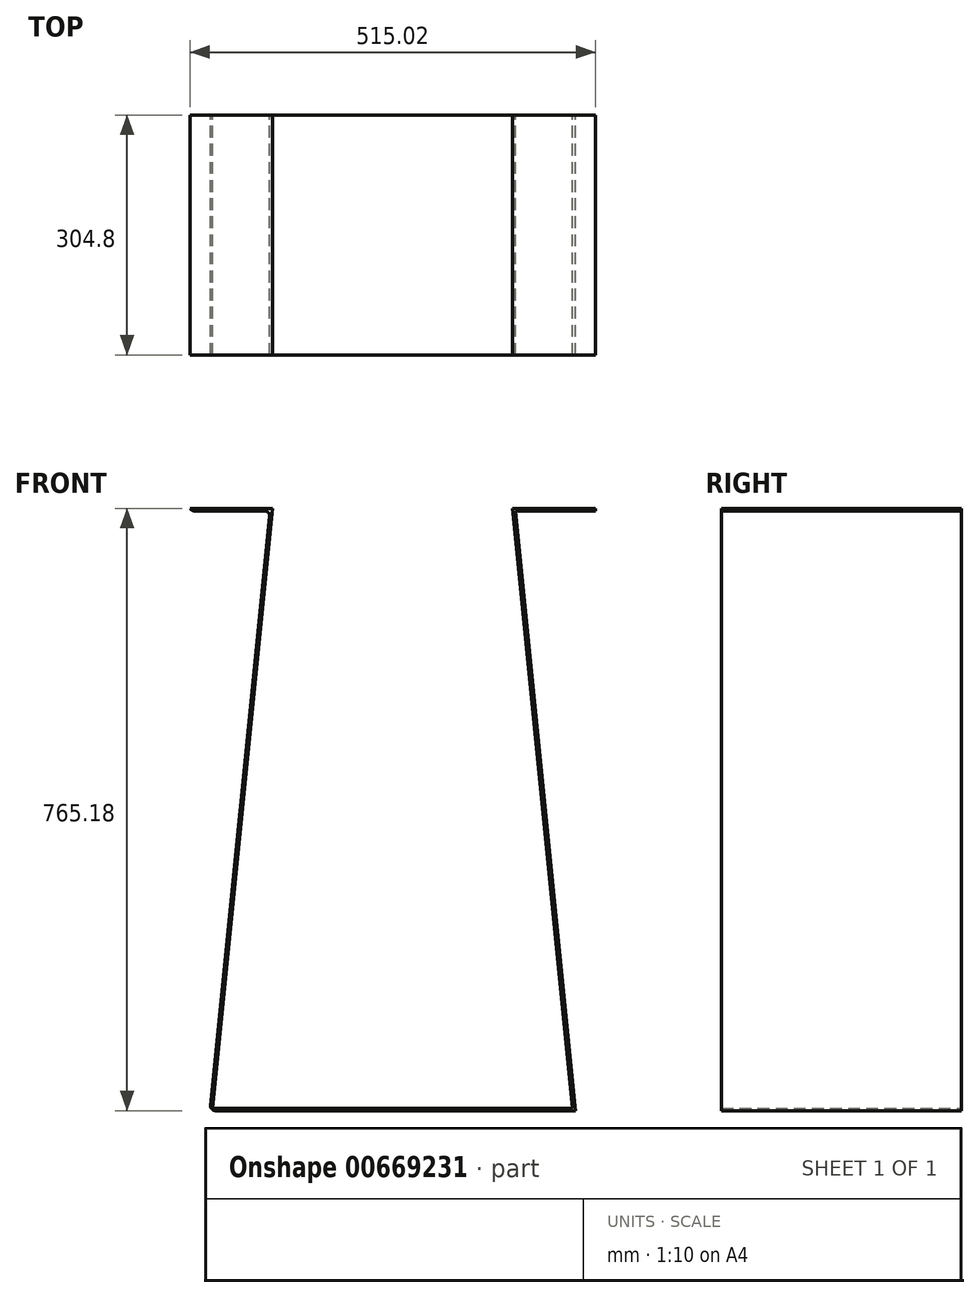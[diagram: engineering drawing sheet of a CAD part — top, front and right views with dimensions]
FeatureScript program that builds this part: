
annotation { "Feature Type Name" : "Feature", "Feature Type Description" : "" }
export const myFeature = defineFeature(function(context is Context, id is Id, definition is map)
    precondition{}
    {
        {
            var Q0;
            Q0=qCreatedBy(makeId("Front.planeOp"),FACE);
            var sketch = newSketch(context, id + "F0", { "sketchPlane" : qUnion([Q0])});
            skLineSegment(sketch, "E0", {"start": v(-232.1, 0) * mm, "end": v(0, 0) * mm});
            skLineSegment(sketch, "E1", {"start": v(-155.9, 762) * mm, "end": v(-257.5, 762) * mm});
            skLineSegment(sketch, "E2", {"start": v(-155.9, 762) * mm, "end": v(-232.1, 0) * mm});
            skLineSegment(sketch, "E3.0", {"start": v(-228.6, 3.17) * mm, "end": v(0, 3.17) * mm});
            skLineSegment(sketch, "E3.1", {"start": v(-152.4, 765.18) * mm, "end": v(-228.6, 3.17) * mm});
            skLineSegment(sketch, "E3.2", {"start": v(-152.4, 765.18) * mm, "end": v(-257.5, 765.18) * mm});
            skLineSegment(sketch, "E4", {"start": v(-257.5, 765.18) * mm, "end": v(-257.5, 762) * mm});
            skLineSegment(sketch, "E5.MirrorCS", {"start": v(257.5, 765.18) * mm, "end": v(257.5, 762) * mm});
            skLineSegment(sketch, "E6.MirrorCS", {"start": v(232.1, 0) * mm, "end": v(0, 0) * mm});
            skLineSegment(sketch, "E7.MirrorCS", {"start": v(155.9, 762) * mm, "end": v(257.5, 762) * mm});
            skLineSegment(sketch, "E8.MirrorCS", {"start": v(155.9, 762) * mm, "end": v(232.1, 0) * mm});
            skLineSegment(sketch, "E9.MirrorCS", {"start": v(152.4, 765.18) * mm, "end": v(257.5, 765.18) * mm});
            skLineSegment(sketch, "E10.MirrorCS", {"start": v(228.6, 3.17) * mm, "end": v(0, 3.17) * mm});
            skLineSegment(sketch, "E11.MirrorCS", {"start": v(152.4, 765.18) * mm, "end": v(228.6, 3.17) * mm});
            skSolve(sketch);
        }
        {
            var Q0;
            Q0 = qSketchRegion(id + "F0", true);
            extrude(context, id + "F1", {"entities" : qUnion([Q0]), "depth" : 304.8 * mm, "offsetDistance" : 25.4 * mm});
        }
        {
            var Q0;
            Q0=makeQuery(id+"F1.opExtrude","SWEPT_EDGE",EDGE,{"disambiguationData":[OSD([sQuery(id+"F0.wireOp",EDGE,"0979d7de-9660-4254-85e0-e3d8d71ecd84.0"),sQuery(id+"F0.wireOp",EDGE,"0979d7de-9660-4254-85e0-e3d8d71ecd84.1")])]});
            var Q1;
            Q1=makeQuery(id+"F1.opExtrude","SWEPT_EDGE",EDGE,{"disambiguationData":[OSD([sQuery(id+"F0.wireOp",EDGE,"0979d7de-9660-4254-85e0-e3d8d71ecd84.2"),sQuery(id+"F0.wireOp",EDGE,"0979d7de-9660-4254-85e0-e3d8d71ecd84.3")])]});
            var Q2;
            Q2=makeQuery(id+"F1.opExtrude","SWEPT_EDGE",EDGE,{"disambiguationData":[OSD([sQuery(id+"F0.wireOp",EDGE,"SrGywmnR-CA1C-95Wa-ZYoq-HhFQO3ZezqlZ"),sQuery(id+"F0.wireOp",EDGE,"E0")])]});
            var Q3;
            Q3=makeQuery(id+"F1.opExtrude","SWEPT_EDGE",EDGE,{"disambiguationData":[OSD([sQuery(id+"F0.wireOp",EDGE,"0979d7de-9660-4254-85e0-e3d8d71ecd84.3"),sQuery(id+"F0.wireOp",EDGE,"0979d7de-9660-4254-85e0-e3d8d71ecd84.4")])]});
            var Q4;
            Q4=makeQuery(id+"F1.opExtrude","SWEPT_EDGE",EDGE,{"disambiguationData":[OSD([sQuery(id+"F0.wireOp",EDGE,"SrGywmnR-CA1C-95Wa-ZYoq-HhFQO3ZezqlZ"),sQuery(id+"F0.wireOp",EDGE,"E1")])]});
            var Q5;
            Q5=makeQuery(id+"F1.opExtrude","SWEPT_EDGE",EDGE,{"disambiguationData":[OSD([sQuery(id+"F0.wireOp",EDGE,"dc26557d-8df7-4877-be75-f5ed8d5301a31.MirrorCS"),sQuery(id+"F0.wireOp",EDGE,"dc26557d-8df7-4877-be75-f5ed8d5301a32.MirrorCS")])]});
            var Q6;
            Q6=makeQuery(id+"F1.opExtrude","SWEPT_EDGE",EDGE,{"disambiguationData":[OSD([sQuery(id+"F0.wireOp",EDGE,"0979d7de-9660-4254-85e0-e3d8d71ecd84.1"),sQuery(id+"F0.wireOp",EDGE,"0979d7de-9660-4254-85e0-e3d8d71ecd84.5")])]});
            var Q7;
            Q7=makeQuery(id+"F1.opExtrude","SWEPT_EDGE",EDGE,{"disambiguationData":[OSD([sQuery(id+"F0.wireOp",EDGE,"dc26557d-8df7-4877-be75-f5ed8d5301a30.MirrorCS"),sQuery(id+"F0.wireOp",EDGE,"dc26557d-8df7-4877-be75-f5ed8d5301a32.MirrorCS")])]});
            fillet(context, id + "F2", {"entities" : qUnion([Q0, Q1, Q2, Q3, Q4, Q5, Q6, Q7]), "radius" : 6.35 * mm, "tangentPropagation" : true, "allowEdgeOverflow" : false});
        }
    });
